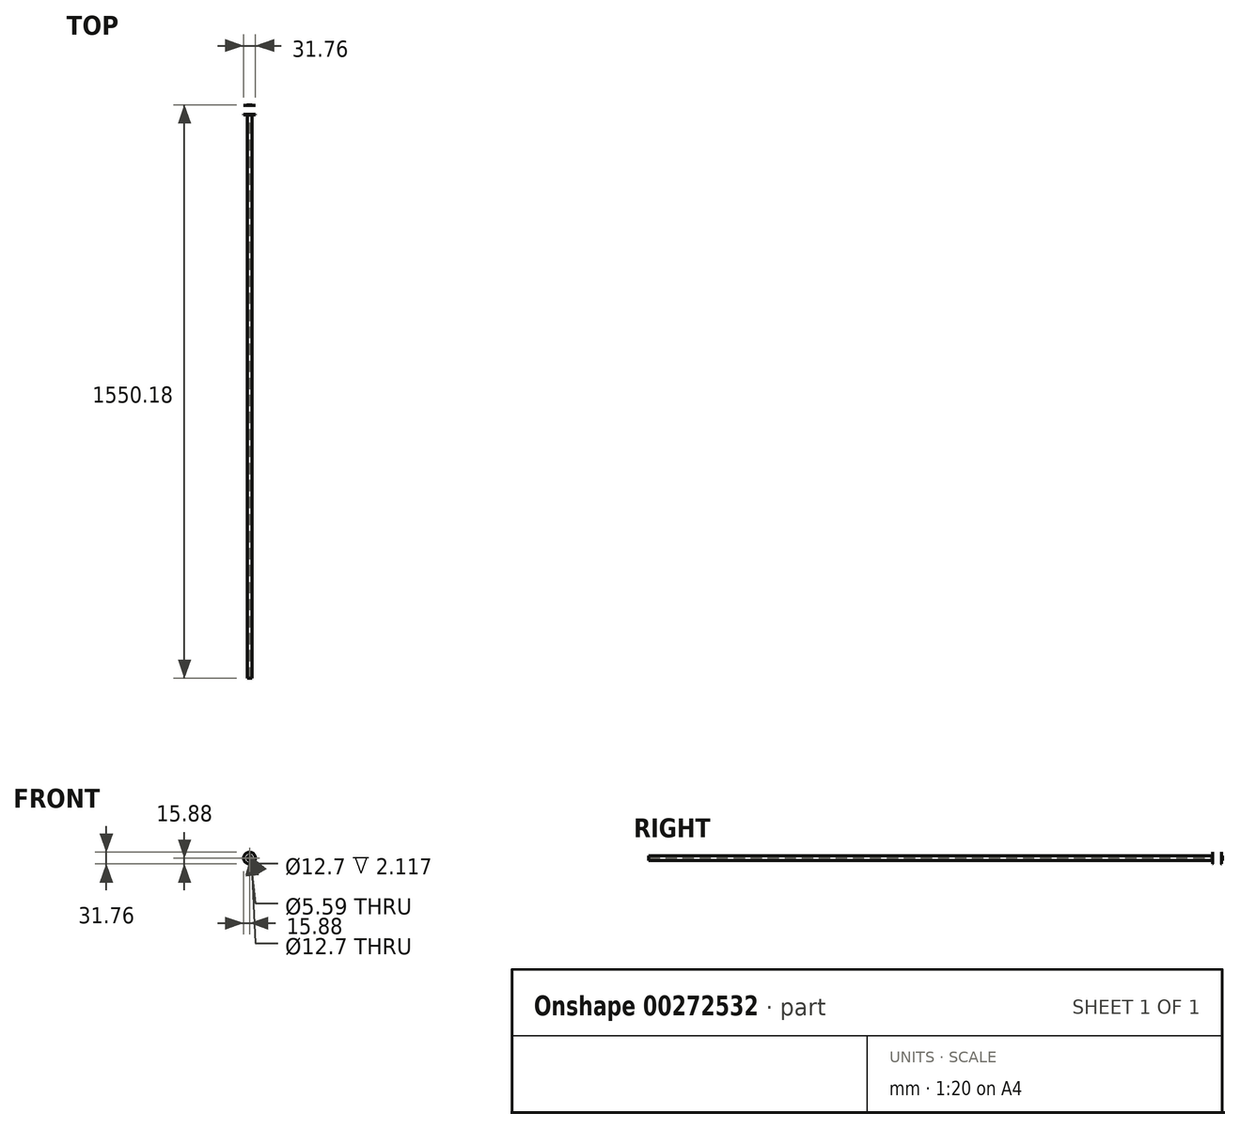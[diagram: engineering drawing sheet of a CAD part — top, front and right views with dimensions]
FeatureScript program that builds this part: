
annotation { "Feature Type Name" : "Feature", "Feature Type Description" : "" }
export const myFeature = defineFeature(function(context is Context, id is Id, definition is map)
    precondition{}
    {
        {
            var Q0;
            Q0=qCreatedBy(makeId("Front.planeOp"),FACE);
            var sketch = newSketch(context, id + "F0", { "sketchPlane" : qUnion([Q0])});
            skCircle(sketch, "E0", {"center": v(0, 0) * mm, "radius": 6.35 * mm});
            skCircle(sketch, "E1.0", {"center": v(0, 0) * mm, "radius": 15.88 * mm});
            skSolve(sketch);
        }
        {
            var Q0;
            Q0=makeQuery(id+"F0.imprint","IMPRINT",FACE,{"disambiguationData":[TD([[makeQuery(id+"F0.imprint","IMPRINT",EDGE,{"derivedFrom":sQuery(id+"F0.wireOp",EDGE,"E0")}),-1.0]])]});
            extrude(context, id + "F1", {"entities" : qUnion([Q0]), "depth" : 0.4 * mm});
        }
        {
            var Q0;
            Q0=qCreatedBy(makeId("Front.planeOp"),FACE);
            var sketch = newSketch(context, id + "F2", { "sketchPlane" : qUnion([Q0])});
            skCircle(sketch, "E2", {"center": v(0, 0) * mm, "radius": 6.35 * mm});
            skCircle(sketch, "E3.0", {"center": v(0, 0) * mm, "radius": 2.8 * mm});
            skSolve(sketch);
        }
        {
            var Q0;
            Q0=makeQuery(id+"F2.imprint","IMPRINT",FACE,{"disambiguationData":[TD([[makeQuery(id+"F2.imprint","IMPRINT",EDGE,{"derivedFrom":sQuery(id+"F2.wireOp",EDGE,"E2")}),1.0]])]});
            extrude(context, id + "F3", {"entities" : qUnion([Q0]), "depth" : 1524 * mm});
        }
        {
            var Q0;
            Q0=qCreatedBy(makeId("Right.planeOp"),FACE);
            var sketch = newSketch(context, id + "F4", { "sketchPlane" : qUnion([Q0])});
            skLineSegment(sketch, "E4", {"start": v(0, 0) * mm, "end": v(50.8, 0) * mm, "construction": true});
            skLineSegment(sketch, "E5", {"start": v(26.18, 6.35) * mm, "end": v(24.06, 6.35) * mm});
            skLineSegment(sketch, "E6", {"start": v(24.06, 6.35) * mm, "end": v(24.06, 15.88) * mm});
            skLineSegment(sketch, "E7.0", {"start": v(24.47, 6.76) * mm, "end": v(24.47, 15.88) * mm});
            skLineSegment(sketch, "E8.0", {"start": v(26.18, 6.76) * mm, "end": v(24.47, 6.76) * mm});
            skLineSegment(sketch, "E9", {"start": v(24.06, 15.88) * mm, "end": v(24.47, 15.88) * mm});
            skLineSegment(sketch, "E10", {"start": v(26.18, 6.76) * mm, "end": v(26.18, 6.35) * mm});
            skSolve(sketch);
        }
        {
            var Q0;
            Q0=makeQuery(id+"F4.imprint","IMPRINT",FACE,{"disambiguationData":[TD([[makeQuery(id+"F4.imprint","IMPRINT",EDGE,{"derivedFrom":sQuery(id+"F4.wireOp",EDGE,"E5")}),-1.0]])]});
            var Q1;
            Q1=sQuery(id+"F4.wireOp",EDGE,"E4");
            revolve(context, id + "F5", {"entities" : qUnion([Q0]), "axis" : qUnion([Q1]), "revolveType" : RevolveType.FULL});
        }
    });
